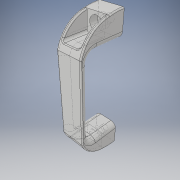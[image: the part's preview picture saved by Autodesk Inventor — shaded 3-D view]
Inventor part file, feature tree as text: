
AUTODESK INVENTOR PART (.ipt)
format: ipt  version: 2019 (Build 230136000, 136)  size: 235,008 bytes
history: native  units: in
note: dims shown in document units (in); Inventor stores cm internally (conversion verified against a paired STEP export)
features: fillet x1
ambient origin geometry x8: Origin, YZ Plane, XZ Plane, XY Plane, X Axis, Y Axis, Z Axis, Center Point
bodies: Solid1 (feature_tree)
feature tree (1):
  fillet  "Fillet3"  [1 undecoded]
note: 1 required parameter value undecoded (feature->parameter linkage not recoverable at this tier; creation-order binding heuristic only, values carry confidence <= 0.55)
